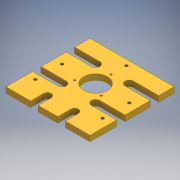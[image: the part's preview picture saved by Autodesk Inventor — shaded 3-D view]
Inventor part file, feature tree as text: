
AUTODESK INVENTOR PART (.ipt)
format: ipt  version: 2016 (Build 200138000, 138)  size: 211,968 bytes
history: native  units: mm
features: sketch x6, extrude x4, mirror x2, hole x2, pattern_linear x1
ambient origin geometry x8: Origin, YZ Plane, XZ Plane, XY Plane, X Axis, Y Axis, Z Axis, Center Point
bodies: Solid1 (feature_tree)
feature tree (15):
  extrude  "baseExtrusion"  Depth=75.0mm
  extrude  "objectiveExtrusion"  Depth=10.0mm TaperAngle=0.0deg
  extrude  "cageRodBase1"  Depth=10.0mm TaperAngle=0.0deg
  mirror  "cageRodBase2"
  pattern_linear  "cageRodBase34"  Count1=2  [1 undecoded]
  hole  "objectiveHolderMountingHoles"  [1 undecoded]
  hole  "m6MountingHoles"  [1 undecoded]
  extrude  "filterWheelPost1"  Depth=75.0mm
  mirror  "filterWheelPost2"
  sketch  "Sketch1"  dims[d0=150.0mm d1=75.0mm]
  sketch  "Sketch3"  dims[d2=150.0mm d4=10.0mm d5=0.0mm]
  sketch  "Sketch5"  dims[d16=42.5mm d18=10.0mm d19=0.0mm]
  sketch  "Sketch8"  dims[d34=15.0mm]
  sketch  "Sketch9"  dims[d35=7.5mm]
  sketch  "Sketch11"  dims[d37=10.0mm d38=0.0mm d40=20.0mm d42=60.0mm d54=30.0mm d67=30.0mm d68=75.0mm d71=75.0mm d72=27.5mm d73=30.0mm d75=360.0deg d77=3.242mm d78=8.0mm d79=4.0mm d80=2.0mm d81=90.0deg d82=11.8mm d83=20.594885mm d84=65.0mm d85=42.5mm d87=120.0mm d88=60.0mm d89=4.917mm d90=12.0mm d91=10.0mm d92=2.0mm d93=90.0deg d94=17.1mm d95=20.594885mm d97=30.0mm d98=55.0mm d99=47.5mm d110=13.5mm d111=30.0mm d112=6.75mm d113=6.75mm d114=24.25mm d115=10.0mm d116=0.0mm]
note: 3 required parameter values undecoded (feature->parameter linkage not recoverable at this tier; creation-order binding heuristic only, values carry confidence <= 0.55)
